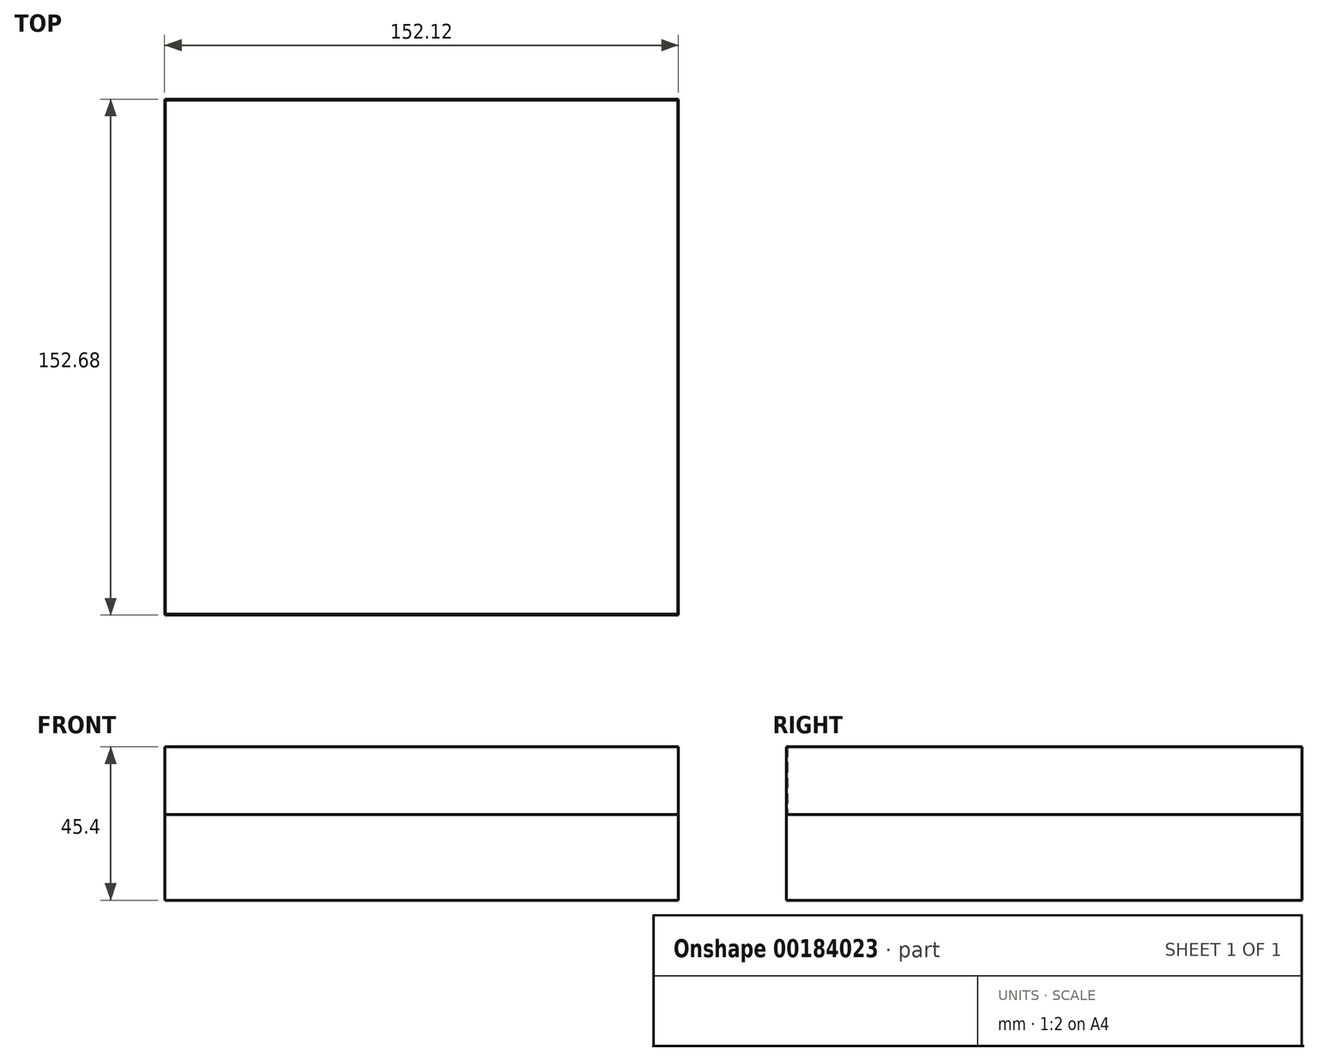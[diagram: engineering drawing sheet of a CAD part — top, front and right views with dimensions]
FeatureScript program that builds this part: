
annotation { "Feature Type Name" : "Feature", "Feature Type Description" : "" }
export const myFeature = defineFeature(function(context is Context, id is Id, definition is map)
    precondition{}
    {
        {
            var Q0;
            Q0=qCreatedBy(makeId("Top.planeOp"),FACE);
            var sketch = newSketch(context, id + "F0", { "sketchPlane" : qUnion([Q0])});
            skLineSegment(sketch, "E0.bottom", {"start": v(75.86, -76.05) * mm, "end": v(-75.86, -76.05) * mm});
            skLineSegment(sketch, "E0.top", {"start": v(75.86, 76.05) * mm, "end": v(-75.86, 76.05) * mm});
            skLineSegment(sketch, "E0.left", {"start": v(75.86, -76.05) * mm, "end": v(75.86, 76.05) * mm});
            skLineSegment(sketch, "E0.right", {"start": v(-75.86, -76.05) * mm, "end": v(-75.86, 76.05) * mm});
            skPoint(sketch, "E0.middle", {"position": v(0, 0) * mm});
            skSolve(sketch);
        }
        {
            var Q0;
            Q0=makeQuery(id+"F0.imprint","IMPRINT",FACE,{"disambiguationData":[TD([[makeQuery(id+"F0.imprint","IMPRINT",EDGE,{"derivedFrom":sQuery(id+"F0.wireOp",EDGE,"E0.bottom")}),-1.0]])]});
            var sketch = newSketch(context, id + "F1", { "sketchPlane" : qUnion([Q0])});
            skLineSegment(sketch, "E1.bottom", {"start": v(76.06, 76.34) * mm, "end": v(-76.06, 76.34) * mm});
            skLineSegment(sketch, "E1.top", {"start": v(76.06, -76.34) * mm, "end": v(-76.06, -76.34) * mm});
            skLineSegment(sketch, "E1.left", {"start": v(76.06, 76.34) * mm, "end": v(76.06, -76.34) * mm});
            skLineSegment(sketch, "E1.right", {"start": v(-76.06, 76.34) * mm, "end": v(-76.06, -76.34) * mm});
            skPoint(sketch, "E1.middle", {"position": v(0, 0) * mm});
            skSolve(sketch);
        }
        {
            var Q0;
            Q0 = qSketchRegion(id + "F1", true);
            var Q1;
            Q1=makeQuery(id+"F0.imprint","IMPRINT",FACE,{"disambiguationData":[TD([[makeQuery(id+"F0.imprint","IMPRINT",EDGE,{"derivedFrom":sQuery(id+"F0.wireOp",EDGE,"E0.bottom")}),-1.0]])]});
            extrude(context, id + "F2", {"entities" : qUnion([Q0, Q1]), "depth" : 20 * mm});
        }
        {
            var Q0;
            Q0=makeQuery(id+"F2.opExtrude","CAP_FACE",FACE,{"disambiguationData":[OSD([sQuery(id+"F1.wireOp",EDGE,"E1.bottom"),sQuery(id+"F1.wireOp",EDGE,"E1.top"),sQuery(id+"F1.wireOp",EDGE,"E1.left"),sQuery(id+"F1.wireOp",EDGE,"E1.right")])],"isStart":true});
            extrude(context, id + "F3", {"entities" : qUnion([Q0]), "depth" : 25.4 * mm});
        }
    });
